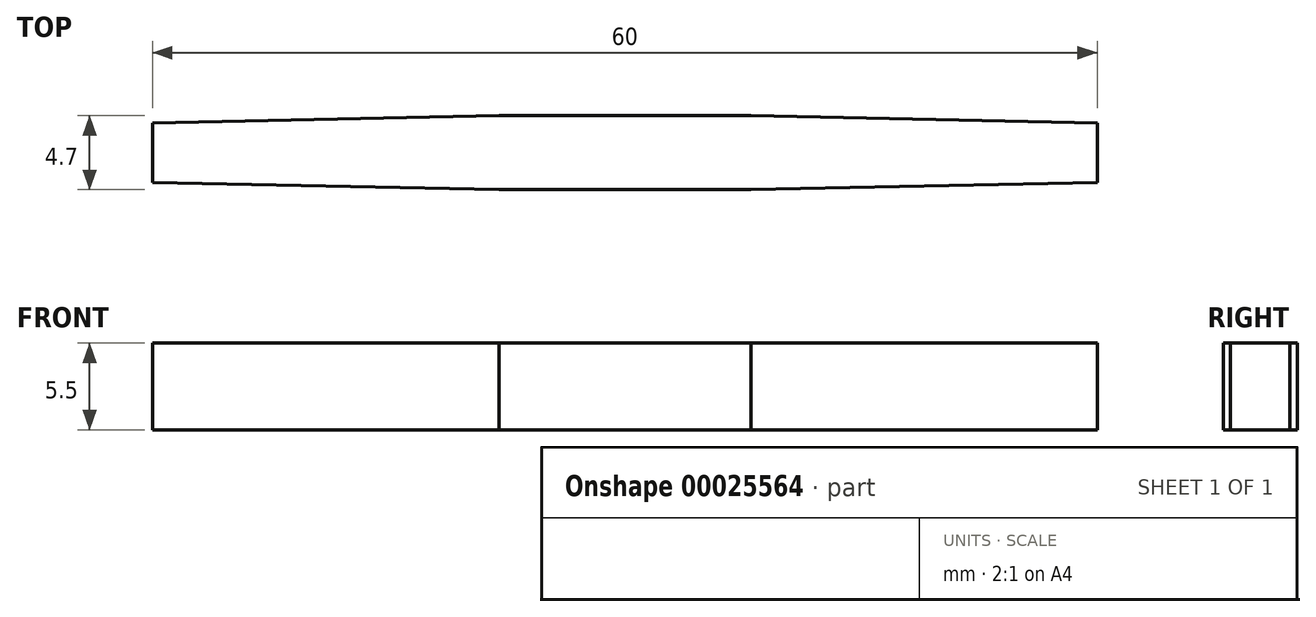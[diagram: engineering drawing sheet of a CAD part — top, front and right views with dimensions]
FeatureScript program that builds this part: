
annotation { "Feature Type Name" : "Feature", "Feature Type Description" : "" }
export const myFeature = defineFeature(function(context is Context, id is Id, definition is map)
    precondition{}
    {
        {
            var Q0;
            Q0=qCreatedBy(makeId("Top.planeOp"),FACE);
            var sketch = newSketch(context, id + "F0", { "sketchPlane" : qUnion([Q0])});
            skPoint(sketch, "E0.rect.middle", {"position": v(0, 0) * mm});
            skLineSegment(sketch, "E1", {"start": v(-8, 2.35) * mm, "end": v(-30, 1.9) * mm});
            skLineSegment(sketch, "E2", {"start": v(-8, -2.35) * mm, "end": v(-30, -1.9) * mm});
            skLineSegment(sketch, "E3", {"start": v(8, 2.35) * mm, "end": v(30, 1.9) * mm});
            skLineSegment(sketch, "E4", {"start": v(8, -2.35) * mm, "end": v(30, -1.9) * mm});
            skLineSegment(sketch, "E5", {"start": v(-8, 2.35) * mm, "end": v(8, 2.35) * mm});
            skLineSegment(sketch, "E6", {"start": v(-8, -2.35) * mm, "end": v(8, -2.35) * mm});
            skLineSegment(sketch, "E7", {"start": v(-30, 1.9) * mm, "end": v(-30, -1.9) * mm});
            skLineSegment(sketch, "E8", {"start": v(30, 1.9) * mm, "end": v(30, -1.9) * mm});
            skSolve(sketch);
        }
        {
            var Q0;
            Q0=makeQuery(id+"F0.imprint","IMPRINT",FACE,{"disambiguationData":[TD([[makeQuery(id+"F0.imprint","IMPRINT",EDGE,{"derivedFrom":sQuery(id+"F0.wireOp",EDGE,"E1")}),1.0]])]});
            extrude(context, id + "F1", {"entities" : qUnion([Q0]), "depth" : 5.5 * mm});
        }
    });
